# Revit family: Lian - Fixed Window - Wood-Aluminium
name_source: partatom
category: Windows
revit_build: Autodesk Revit 2017 (Build: 20181011_1645(x64)
units: mm (PartAtom-declared; Revit-internal decimal feet)

## family parameters
Always vertical = Yes
Cut with Voids When Loaded = No
Host = Wall
Room Calculation Point = No
Shared = No

## types (1)
- Lian - Fixed Window - Wood-Aluminium
    01 - Opening Height = 1200 mm
    01.5 - Window Height = 1180 mm  [stored 3.87139 ft]
    02 - Opening Width = 1400 mm  [stored 4.59318 ft]
    02.5 - Window Width = 1380 mm  [stored 4.52756 ft]
    05.1 - Material Exterior Frame = RAL 9018
    05.2 - Material Interior Frame = NCS S 0500-N
    05.5 - Material Glass = Glass
    07 - Offset = 0 mm  [stored 0 ft]
    08 - Sealant Gap = 10 mm  [stored 0.0328084 ft]
    Analytic Construction = <None>
    GAP = 20 mm  [stored 0.0656168 ft]
    Height = 1180 mm  [stored 3.87139 ft]
    Manufacturer = Lian
    Model = Fixed Window
    OFS = 1500 mm  [stored 4.92126 ft]
    Rough Height = 1200 mm
    Rough Width = 1400 mm  [stored 4.59318 ft]
    Type Comments = Wood - Aluminium
    Type Image = <None>
    URL = http://www.lian.no
    Width = 1380 mm  [stored 4.52756 ft]
    hosted on bimbear.com® = www.bimbear.com

note: [stored X ft] marks values corroborated as IEEE doubles in the binary element streams (Revit-internal decimal feet)

## geometry (parser evidence)
native form markers: Sweep x2
no freeform markers — native parametric forms only
